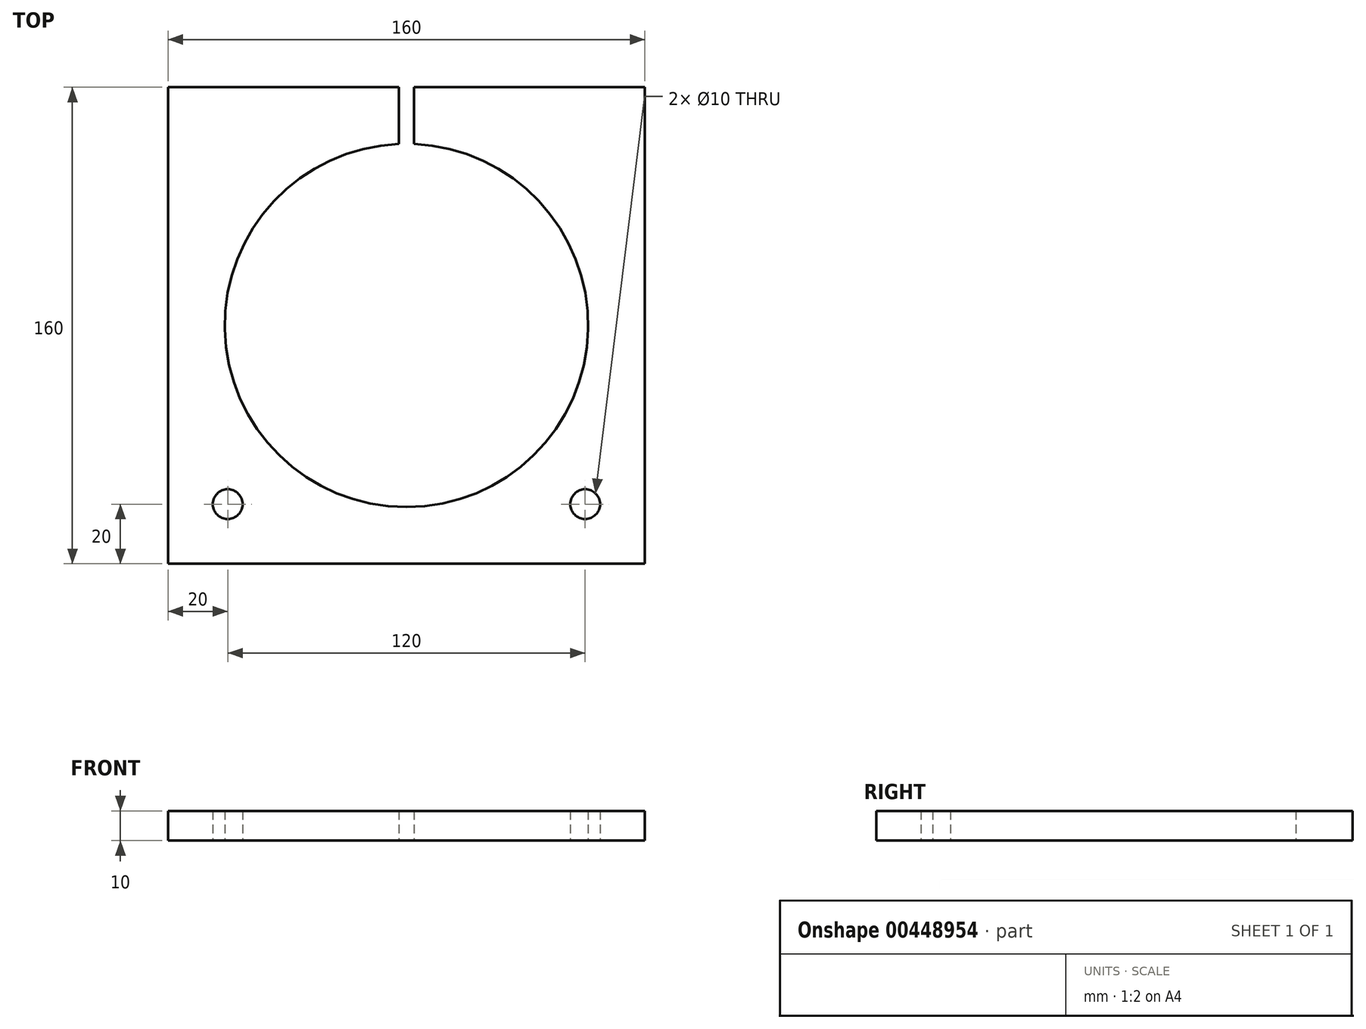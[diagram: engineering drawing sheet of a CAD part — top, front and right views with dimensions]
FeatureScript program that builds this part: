
annotation { "Feature Type Name" : "Feature", "Feature Type Description" : "" }
export const myFeature = defineFeature(function(context is Context, id is Id, definition is map)
    precondition{}
    {
        {
            var Q0;
            Q0=qCreatedBy(makeId("Top.planeOp"),FACE);
            var sketch = newSketch(context, id + "F0", { "sketchPlane" : qUnion([Q0])});
            skLineSegment(sketch, "E0.bottom", {"start": v(-80, -80) * mm, "end": v(80, -80) * mm});
            skLineSegment(sketch, "E0.top", {"start": v(-80, 80) * mm, "end": v(-2.5, 80) * mm});
            skLineSegment(sketch, "E0.left", {"start": v(-80, -80) * mm, "end": v(-80, 80) * mm});
            skLineSegment(sketch, "E0.right", {"start": v(80, -80) * mm, "end": v(80, 80) * mm});
            skPoint(sketch, "E0.middle", {"position": v(0, 0) * mm});
            skLineSegment(sketch, "E1.bottom", {"start": v(-60, -60) * mm, "end": v(60, -60) * mm});
            skLineSegment(sketch, "E1.top", {"start": v(-60, 60) * mm, "end": v(-11, 60) * mm});
            skLineSegment(sketch, "E1.left", {"start": v(-60, -60) * mm, "end": v(-60, 60) * mm});
            skLineSegment(sketch, "E1.right", {"start": v(60, -60) * mm, "end": v(60, 60) * mm});
            skArc(sketch, "E2", {"start": v(-2.5, 60.95) * mm, "mid": v(0, -61) * mm, "end": v(2.5, 60.95) * mm});
            skCircle(sketch, "E3", {"center": v(-60, -60) * mm, "radius": 5 * mm});
            skCircle(sketch, "E4", {"center": v(60, -60) * mm, "radius": 5 * mm});
            skLineSegment(sketch, "E5.left", {"start": v(2.5, 60) * mm, "end": v(2.5, 80) * mm});
            skLineSegment(sketch, "E5.right", {"start": v(-2.5, 50) * mm, "end": v(-2.5, 80) * mm});
            skPoint(sketch, "E5.middle", {"position": v(0, 80) * mm});
            skPoint(sketch, "E5.top.end.orphan", {"position": v(-2.5, 110) * mm});
            skPoint(sketch, "E5.top.start.orphan", {"position": v(2.5, 110) * mm});
            skLineSegment(sketch, "E6.trimOffspring", {"start": v(2.5, 80) * mm, "end": v(80, 80) * mm});
            skLineSegment(sketch, "E7.trimOffspring", {"start": v(11, 60) * mm, "end": v(60, 60) * mm});
            skPoint(sketch, "E8.orphan", {"position": v(2.5, 50) * mm});
            skSolve(sketch);
        }
        {
            var Q0;
            Q0=makeQuery(id+"F0.imprint","IMPRINT",FACE,{"disambiguationData":[TD([[makeQuery(id+"F0.imprint","IMPRINT",EDGE,{"derivedFrom":sQuery(id+"F0.wireOp",EDGE,"E0.bottom")}),1.0]])]});
            var Q1;
            {var subQ0=sQuery(id+"F0.wireOp",EDGE,"E2");var subQ1=sQuery(id+"F0.wireOp",EDGE,"E1.bottom");var subQ2=makeQuery(id+"F0.imprint","INTERSECT",VERTEX,{"disambiguationData":[OD(1.0)],"derivedFrom":[subQ1,subQ0]});Q1=makeQuery(id+"F0.imprint","IMPRINT",FACE,{"disambiguationData":[TD([[makeQuery(id+"F0.imprint","IMPRINT",EDGE,{"disambiguationData":[TD([[subQ2,-1.0]])],"derivedFrom":subQ1}),1.0]])]});}
            var Q2;
            {var subQ0=sQuery(id+"F0.wireOp",EDGE,"E2");var subQ1=sQuery(id+"F0.wireOp",EDGE,"E1.bottom");var subQ2=makeQuery(id+"F0.imprint","INTERSECT",VERTEX,{"disambiguationData":[OD(0.0)],"derivedFrom":[subQ1,subQ0]});Q2=makeQuery(id+"F0.imprint","IMPRINT",FACE,{"disambiguationData":[TD([[makeQuery(id+"F0.imprint","IMPRINT",EDGE,{"disambiguationData":[TD([[subQ2,1.0]])],"derivedFrom":subQ1}),1.0]])]});}
            var Q3;
            {var subQ0=sQuery(id+"F0.wireOp",EDGE,"E1.top");Q3=makeQuery(id+"F0.imprint","IMPRINT",FACE,{"disambiguationData":[TD([[makeQuery(id+"F0.imprint","IMPRINT",EDGE,{"derivedFrom":subQ0}),-1.0]])]});}
            var Q4;
            {var subQ0=sQuery(id+"F0.wireOp",EDGE,"E7.trimOffspring");Q4=makeQuery(id+"F0.imprint","IMPRINT",FACE,{"disambiguationData":[TD([[makeQuery(id+"F0.imprint","IMPRINT",EDGE,{"derivedFrom":subQ0}),-1.0]])]});}
            extrude(context, id + "F1", {"entities" : qUnion([Q0, Q1, Q2, Q3, Q4]), "depth" : 10 * mm});
        }
    });
